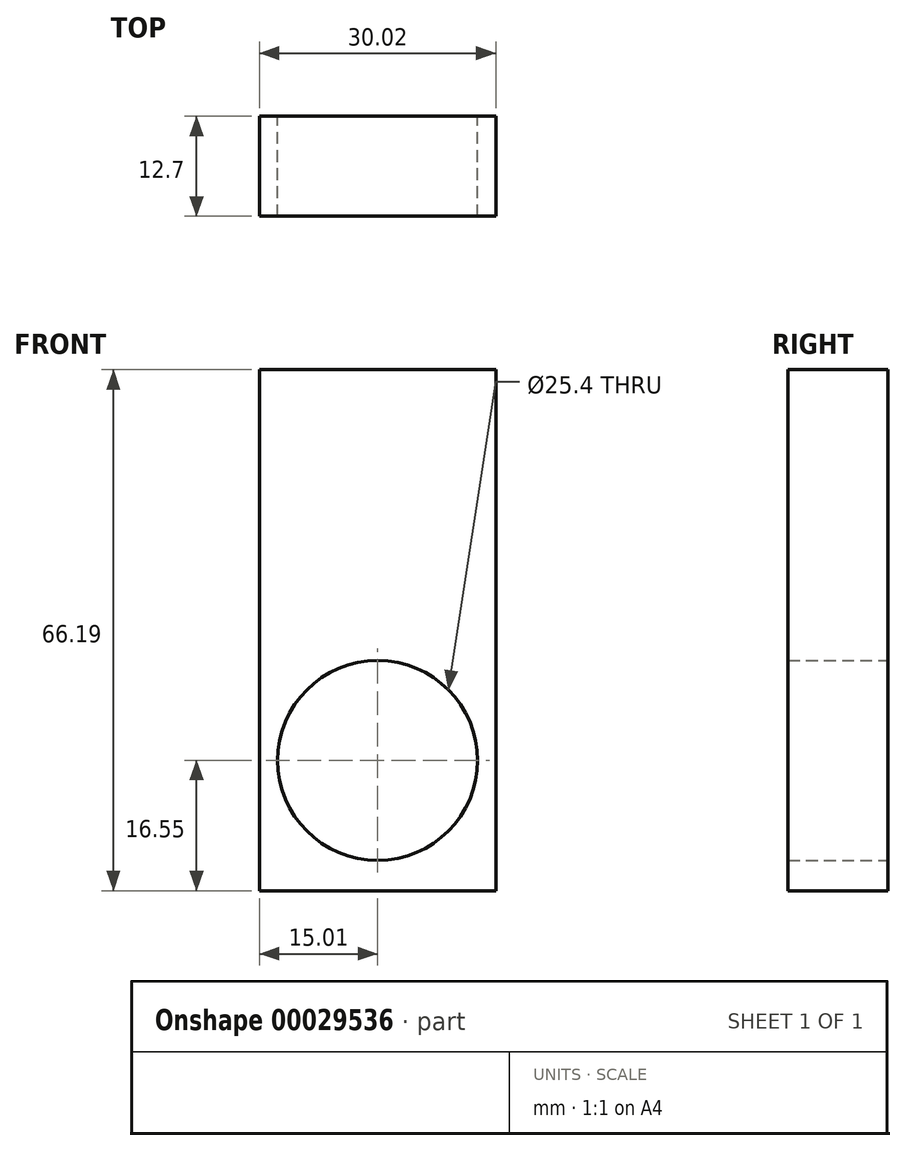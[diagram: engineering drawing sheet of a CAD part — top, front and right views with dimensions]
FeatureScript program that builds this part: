
annotation { "Feature Type Name" : "Feature", "Feature Type Description" : "" }
export const myFeature = defineFeature(function(context is Context, id is Id, definition is map)
    precondition{}
    {
        {
            var Q0;
            Q0=qCreatedBy(makeId("Front.planeOp"),FACE);
            var sketch = newSketch(context, id + "F0", { "sketchPlane" : qUnion([Q0])});
            skCircle(sketch, "E0", {"center": v(0, 0) * mm, "radius": 12.7 * mm});
            skLineSegment(sketch, "E1.rect.bottom", {"start": v(15.01, 49.64) * mm, "end": v(-15.01, 49.64) * mm});
            skLineSegment(sketch, "E1.rect.left", {"start": v(15.01, 49.64) * mm, "end": v(15.01, -16.55) * mm});
            skLineSegment(sketch, "E1.rect.right", {"start": v(-15.01, 49.64) * mm, "end": v(-15.01, -16.55) * mm});
            skLineSegment(sketch, "E2", {"start": v(-15.01, -16.55) * mm, "end": v(15.01, -16.55) * mm});
            skPoint(sketch, "E1.rect.top.end.orphan", {"position": v(-15.01, -49.64) * mm});
            skPoint(sketch, "E3.orphan", {"position": v(15.01, -49.64) * mm});
            skSolve(sketch);
        }
        {
            var Q0;
            Q0=makeQuery(id+"F0.imprint","IMPRINT",FACE,{"disambiguationData":[TD([[makeQuery(id+"F0.imprint","IMPRINT",EDGE,{"derivedFrom":sQuery(id+"F0.wireOp",EDGE,"E0")}),-1.0]])]});
            extrude(context, id + "F1", {"entities" : qUnion([Q0]), "depth" : 12.7 * mm});
        }
    });
